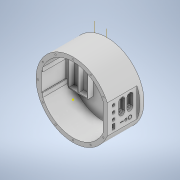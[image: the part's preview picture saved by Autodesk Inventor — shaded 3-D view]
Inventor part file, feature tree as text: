
AUTODESK INVENTOR PART (.ipt)
format: ipt  version: 2020.3 (Build 243373000, 373)  size: 481,792 bytes
history: native  units: mm
features: sketch x23, extrude x21, pattern_linear x3, other x3, pattern_circular x1
ambient origin geometry x8: Origin, YZ Plane, XZ Plane, XY Plane, X Axis, Y Axis, Z Axis, Center Point
bodies: Solid1 (feature_tree)
feature tree (51):
  extrude  "Extrusion1"  Depth=10.0mm TaperAngle=0.0deg
  extrude  "Extrusion2"  Depth=70.0mm
  extrude  "Extrusion4"  Depth=10.0mm
  extrude  "Extrusion7"  Depth=10.0mm TaperAngle=0.0deg
  extrude  "Extrusion8"  Depth=5.9mm
  extrude  "Extrusion9"  Depth=7.0mm
  pattern_linear  "Rectangular Pattern1"  Count1=2  [1 undecoded]
  sketch  "Sketch12"  dims[d36=12.6mm d37=7.0mm]
  extrude  "Extrusion10"  Depth=14.8mm
  extrude  "Extrusion11"  Depth=24.0mm
  extrude  "Extrusion12"  Depth=5.0mm TaperAngle=0.0deg
  extrude  "Extrusion13"  Depth=2.7mm
  extrude  "Extrusion14"  Depth=10.0mm TaperAngle=0.0deg
  extrude  "Extrusion15"  Depth=6.0mm
  extrude  "Extrusion16"  Depth=6.5mm
  extrude  "Extrusion17"  Depth=6.0mm
  pattern_circular  "Circular Pattern2"  [2 undecoded]
  extrude  "Extrusion18"  Depth=10.0mm
  extrude  "Extrusion19"  Depth=10.0mm
  pattern_linear  "Rectangular Pattern2"  Spacing1=10.0mm  [1 undecoded]
  extrude  "Extrusion20"  Depth=7.0mm TaperAngle=0.0deg
  extrude  "Extrusion21"  Depth=1.5mm
  sketch  "Sketch28"  dims[d58=2.7mm d59=10.0mm d60=0.0mm]
  extrude  "Extrusion23"  Depth=8.0mm
  extrude  "Extrusion24"  Depth=7.0mm
  extrude  "Extrusion25"  Depth=9.0mm
  pattern_linear  "Rectangular Pattern3"  Spacing1=10.0mm  [1 undecoded]
  sketch  "Sketch32"  dims[d70=6.0mm d71=5.0mm d72=0.0mm d73=10.0mm d74=10.0mm d75=10.0mm d76=7.0mm d77=0.0mm d78=1.5mm d79=8.0mm d80=7.0mm d81=9.0mm d82=10.0mm d83=10.0mm d84=1.0mm d85=0.0mm d86=21.2mm d87=21.2mm d88=75.6mm d89=75.6mm d90=2.0mm d91=2.0mm d92=2.0mm d93=2.0mm d94=2.0mm d95=23.0mm d96=13.0mm d97=0.0mm d98=2.0mm d99=1.5mm d100=1.5mm d101=2.0mm d102=1.5mm d103=1.5mm d104=2.0mm d105=0.0mm d106=2.0mm d107=2.0mm d108=1.5mm d109=1.5mm d110=1.5mm d111=1.5mm d112=2.0mm d113=0.0mm d114=85.0mm d115=3.2mm d116=30.0deg d117=100.0mm d118=0.0mm d122=6.0mm d123=54.0mm d124=0.0mm d125=110.0mm d126=300.0deg d128=2.7mm d129=54.0mm d130=4.0mm d131=21.2mm d132=75.6mm d134=2.0mm d135=2.0mm d136=2.0mm d137=2.0mm d138=23.0mm d139=10.0mm d140=0.0mm d141=1.6mm d142=4.0mm d143=15.5mm d144=15.5mm d145=10.0mm d146=0.0mm d147=20.0mm d149=31.0mm d150=20.0mm d152=31.0mm d153=2.0mm d154=1.5mm d155=1.5mm d156=10.0mm d157=0.0mm d158=2.0mm d159=1.5mm d160=1.5mm d161=10.0mm d162=0.0mm d176=45.3mm d177=1.4mm d178=2.0mm d179=1.0mm d180=1.0mm d181=1.4mm d182=2.0mm d183=10.0mm d184=0.0mm d185=10.0mm d186=0.0mm d187=3.5mm d188=4.0mm d189=0.0mm d190=20.0mm d192=31.0mm d193=20.0mm d195=31.0mm]
  sketch  "Sketch1"  dims[d0=180.0mm d1=10.0mm d2=0.0mm]
  sketch  "Sketch2"  dims[d3=42.0mm d4=70.0mm]
  sketch  "Sketch8"  dims[d5=90.0mm d7=10.0mm]
  sketch  "Sketch9"  dims[d8=72.0mm d9=0.0mm d20=10.0mm d21=0.0mm]
  sketch  "Sketch11"  dims[d34=10.0mm d35=5.9mm]
  sketch  "Sketch13"  dims[d38=7.0mm]
  sketch  "Sketch14"  dims[d39=7.0mm]
  sketch  "Sketch15"  dims[d41=15.0mm]
  sketch  "Sketch16"  dims[d42=15.0mm]
  sketch  "Sketch17"  dims[d43=15.0mm]
  sketch  "Sketch18"  dims[d44=12.5mm]
  sketch  "Sketch19"  dims[d45=15.0mm]
  sketch  "Sketch20"  dims[d46=2.95mm d47=20.0mm]
  sketch  "Sketch22"  dims[d48=10.0mm d49=0.0mm d50=14.8mm]
  sketch  "Sketch23"  dims[d51=24.0mm d52=25.0mm]
  sketch  "Sketch24"  dims[d53=20.0mm d54=5.0mm d55=0.0mm]
  sketch  "Sketch25"  dims[d56=29.0mm d57=2.7mm]
  sketch  "Sketch29"  dims[d61=20.0mm d63=20.0mm d64=6.0mm]
  sketch  "Sketch30"  dims[d66=30.0mm d67=6.5mm]
  sketch  "Sketch31"  dims[d68=6.5mm d69=6.0mm]
  other  "Work Axis1"
  other  "Work Axis2"
  other  "Work Axis3"
note: 5 required parameter values undecoded (feature->parameter linkage not recoverable at this tier; creation-order binding heuristic only, values carry confidence <= 0.55)
